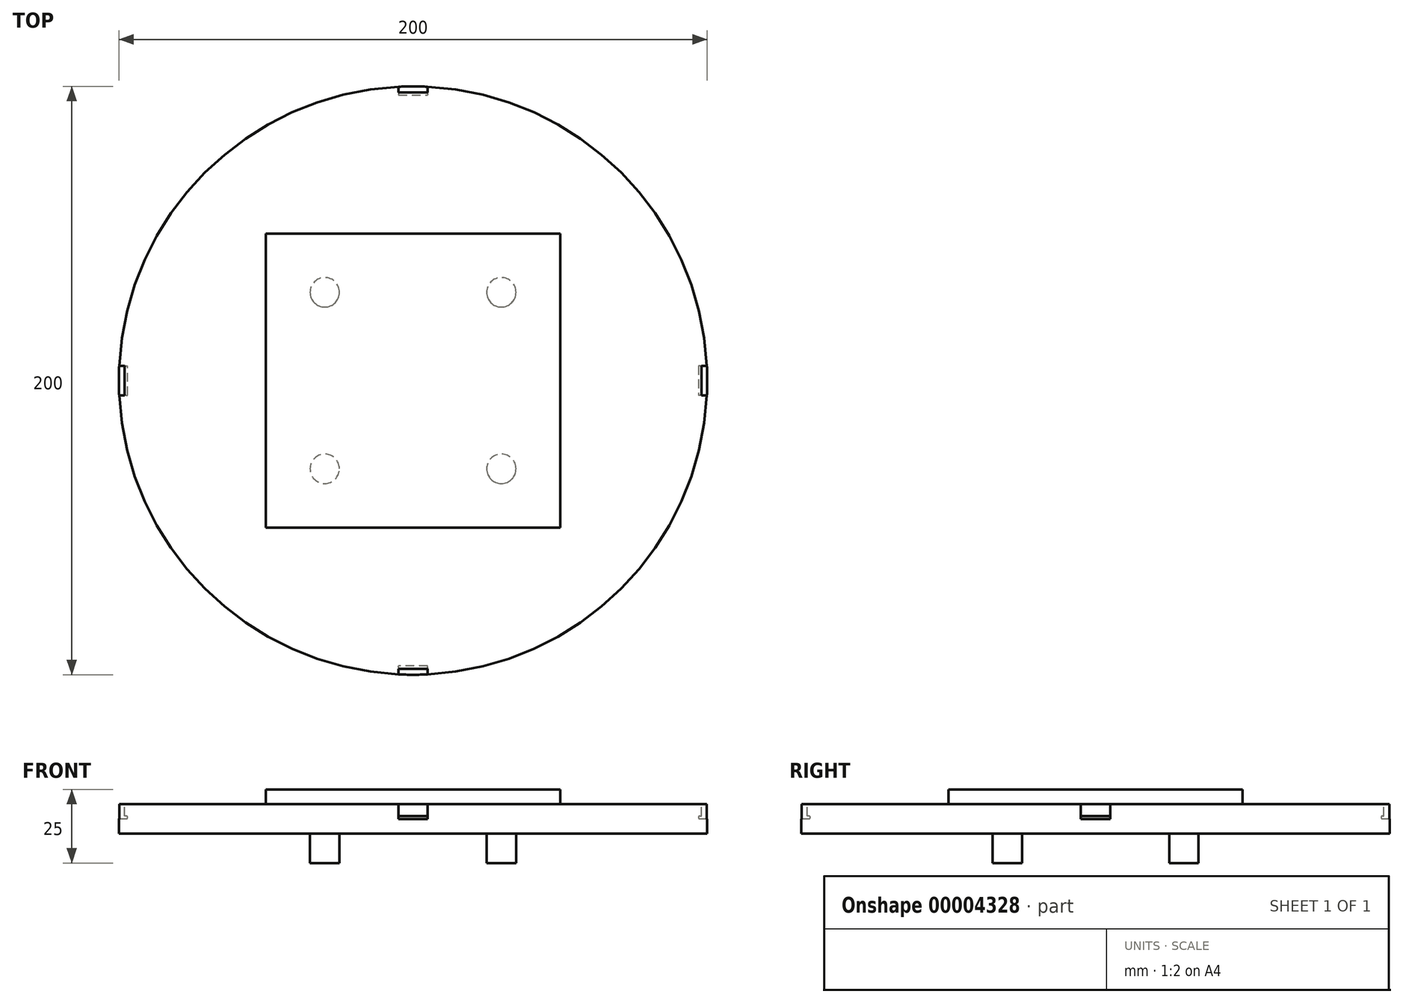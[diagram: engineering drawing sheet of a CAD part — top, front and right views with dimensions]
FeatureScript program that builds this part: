
annotation { "Feature Type Name" : "Feature", "Feature Type Description" : "" }
export const myFeature = defineFeature(function(context is Context, id is Id, definition is map)
    precondition{}
    {
        {
            var Q0;
            Q0=qCreatedBy(makeId("Top.planeOp"),FACE);
            var sketch = newSketch(context, id + "F0", { "sketchPlane" : qUnion([Q0])});
            skCircle(sketch, "E0", {"center": v(0, 0) * mm, "radius": 100 * mm});
            skSolve(sketch);
        }
        {
            var Q0;
            Q0=makeQuery(id+"F0.imprint","IMPRINT",FACE,{"disambiguationData":[TD([[makeQuery(id+"F0.imprint","IMPRINT",EDGE,{"derivedFrom":sQuery(id+"F0.wireOp",EDGE,"E0")}),1.0]])]});
            extrude(context, id + "F1", {"entities" : qUnion([Q0]), "depth" : 10 * mm});
        }
        {
            var Q0;
            Q0=makeQuery(id+"F1.opExtrude","CAP_FACE",FACE,{"disambiguationData":[OSD([sQuery(id+"F0.wireOp",EDGE,"E0")])],"isStart":false});
            var sketch = newSketch(context, id + "F2", { "sketchPlane" : qUnion([Q0])});
            skCircle(sketch, "E1.0", {"center": v(0, 0) * mm, "radius": 90 * mm});
            skLineSegment(sketch, "E2.0", {"start": v(50, 50) * mm, "end": v(-50, 50) * mm});
            skLineSegment(sketch, "E3.0", {"start": v(50, -50) * mm, "end": v(-50, -50) * mm});
            skLineSegment(sketch, "E4.trimOffspring", {"start": v(-50, -50) * mm, "end": v(-50, 50) * mm});
            skLineSegment(sketch, "E5.trimOffspring", {"start": v(50, -50) * mm, "end": v(50, 50) * mm});
            skSolve(sketch);
        }
        {
            var Q0;
            Q0=makeQuery(id+"F1.opExtrude","CAP_FACE",FACE,{"disambiguationData":[OSD([sQuery(id+"F0.wireOp",EDGE,"E0")])],"isStart":false});
            var sketch = newSketch(context, id + "F3", { "sketchPlane" : qUnion([Q0])});
            skLineSegment(sketch, "E6.0", {"start": v(5, -98) * mm, "end": v(-5, -98) * mm});
            skLineSegment(sketch, "E7", {"start": v(-5, -98) * mm, "end": v(-5, -101) * mm});
            skLineSegment(sketch, "E8", {"start": v(5, -98) * mm, "end": v(5, -101) * mm});
            skLineSegment(sketch, "E9.0", {"start": v(-98, 5) * mm, "end": v(-98, -5) * mm});
            skLineSegment(sketch, "E10", {"start": v(-98, 5) * mm, "end": v(-101, 5) * mm});
            skLineSegment(sketch, "E11", {"start": v(-98, -5) * mm, "end": v(-101, -5) * mm});
            skLineSegment(sketch, "E12.0", {"start": v(5, 98) * mm, "end": v(-5, 98) * mm});
            skLineSegment(sketch, "E13", {"start": v(-5, 101) * mm, "end": v(-5, 98) * mm});
            skLineSegment(sketch, "E14", {"start": v(5, 101) * mm, "end": v(5, 98) * mm});
            skLineSegment(sketch, "E15.0", {"start": v(98, 5) * mm, "end": v(98, -5) * mm});
            skLineSegment(sketch, "E16", {"start": v(101, 5) * mm, "end": v(98, 5) * mm});
            skLineSegment(sketch, "E17", {"start": v(101, -5) * mm, "end": v(98, -5) * mm});
            skLineSegment(sketch, "E18.0", {"start": v(-101, 5) * mm, "end": v(-101, -5) * mm});
            skLineSegment(sketch, "E19.0", {"start": v(5, 101) * mm, "end": v(-5, 101) * mm});
            skLineSegment(sketch, "E20.0", {"start": v(101, 5) * mm, "end": v(101, -5) * mm});
            skLineSegment(sketch, "E21.0", {"start": v(5, -101) * mm, "end": v(-5, -101) * mm});
            skSolve(sketch);
        }
        {
            var Q0;
            Q0=makeQuery(id+"F2.imprint","IMPRINT",FACE,{"disambiguationData":[TD([[makeQuery(id+"F2.imprint","IMPRINT",EDGE,{"derivedFrom":sQuery(id+"F2.wireOp",EDGE,"E2.0")}),1.0]])]});
            extrude(context, id + "F4", {"entities" : qUnion([Q0]), "operationType" : NewBodyOperationType.ADD, "depth" : 5 * mm});
        }
        {
            var Q0;
            {var subQ5=sQuery(id+"F3.wireOp",EDGE,"E12.0");Q0=makeQuery(id+"F3.imprint","IMPRINT",FACE,{"disambiguationData":[TD([[makeQuery(id+"F3.imprint","IMPRINT",EDGE,{"derivedFrom":subQ5}),-1.0]])]});}
            var Q1;
            {var subQ5=sQuery(id+"F3.wireOp",EDGE,"E9.0");Q1=makeQuery(id+"F3.imprint","IMPRINT",FACE,{"disambiguationData":[TD([[makeQuery(id+"F3.imprint","IMPRINT",EDGE,{"derivedFrom":subQ5}),-1.0]])]});}
            var Q2;
            {var subQ5=sQuery(id+"F3.wireOp",EDGE,"E6.0");Q2=makeQuery(id+"F3.imprint","IMPRINT",FACE,{"disambiguationData":[TD([[makeQuery(id+"F3.imprint","IMPRINT",EDGE,{"derivedFrom":subQ5}),1.0]])]});}
            var Q3;
            {var subQ5=sQuery(id+"F3.wireOp",EDGE,"E15.0");Q3=makeQuery(id+"F3.imprint","IMPRINT",FACE,{"disambiguationData":[TD([[makeQuery(id+"F3.imprint","IMPRINT",EDGE,{"derivedFrom":subQ5}),1.0]])]});}
            extrude(context, id + "F5", {"entities" : qUnion([Q0, Q1, Q2, Q3]), "operationType" : NewBodyOperationType.REMOVE, "oppositeDirection" : true, "depth" : 5 * mm});
        }
        {
            var Q0;
            Q0=makeQuery(id+"F5.boolean.opBoolean","COPY",FACE,{"derivedFrom":makeQuery(id+"F5.opExtrude","SWEPT_FACE",FACE,{"disambiguationData":[OSD([sQuery(id+"F3.wireOp",EDGE,"E15.0")])]})});
            var sketch = newSketch(context, id + "F6", { "sketchPlane" : qUnion([Q0])});
            skLineSegment(sketch, "E22.0", {"start": v(5, 6) * mm, "end": v(-5, 6) * mm});
            skSolve(sketch);
        }
        {
            var Q0;
            Q0=makeQuery(id+"F5.boolean.opBoolean","COPY",FACE,{"derivedFrom":makeQuery(id+"F5.opExtrude","SWEPT_FACE",FACE,{"disambiguationData":[OSD([sQuery(id+"F3.wireOp",EDGE,"E6.0")])]})});
            var sketch = newSketch(context, id + "F7", { "sketchPlane" : qUnion([Q0])});
            skLineSegment(sketch, "E23.0", {"start": v(5, 6) * mm, "end": v(-5, 6) * mm});
            skSolve(sketch);
        }
        {
            var Q0;
            Q0=makeQuery(id+"F5.boolean.opBoolean","COPY",FACE,{"derivedFrom":makeQuery(id+"F5.opExtrude","SWEPT_FACE",FACE,{"disambiguationData":[OSD([sQuery(id+"F3.wireOp",EDGE,"E9.0")])]})});
            var sketch = newSketch(context, id + "F8", { "sketchPlane" : qUnion([Q0])});
            skLineSegment(sketch, "E24.0", {"start": v(-5, 6) * mm, "end": v(5, 6) * mm});
            skSolve(sketch);
        }
        {
            var Q0;
            Q0=makeQuery(id+"F5.boolean.opBoolean","COPY",FACE,{"derivedFrom":makeQuery(id+"F5.opExtrude","SWEPT_FACE",FACE,{"disambiguationData":[OSD([sQuery(id+"F3.wireOp",EDGE,"E12.0")])]})});
            var sketch = newSketch(context, id + "F9", { "sketchPlane" : qUnion([Q0])});
            skLineSegment(sketch, "E25.0", {"start": v(-5, 6) * mm, "end": v(5, 6) * mm});
            skSolve(sketch);
        }
        {
            var Q0;
            {var subQ2=sQuery(id+"F9.wireOp",EDGE,"E25.0");Q0=makeQuery(id+"F9.imprint","IMPRINT",FACE,{"disambiguationData":[TD([[makeQuery(id+"F9.imprint","IMPRINT",EDGE,{"derivedFrom":subQ2}),-1.0]])]});}
            extrude(context, id + "F10", {"entities" : qUnion([Q0]), "operationType" : NewBodyOperationType.REMOVE, "oppositeDirection" : true, "depth" : 1 * mm});
        }
        {
            var Q0;
            {var subQ2=sQuery(id+"F8.wireOp",EDGE,"E24.0");Q0=makeQuery(id+"F8.imprint","IMPRINT",FACE,{"disambiguationData":[TD([[makeQuery(id+"F8.imprint","IMPRINT",EDGE,{"derivedFrom":subQ2}),-1.0]])]});}
            extrude(context, id + "F11", {"entities" : qUnion([Q0]), "operationType" : NewBodyOperationType.REMOVE, "oppositeDirection" : true, "depth" : 1 * mm});
        }
        {
            var Q0;
            {var subQ2=sQuery(id+"F7.wireOp",EDGE,"E23.0");Q0=makeQuery(id+"F7.imprint","IMPRINT",FACE,{"disambiguationData":[TD([[makeQuery(id+"F7.imprint","IMPRINT",EDGE,{"derivedFrom":subQ2}),1.0]])]});}
            extrude(context, id + "F12", {"entities" : qUnion([Q0]), "operationType" : NewBodyOperationType.REMOVE, "oppositeDirection" : true, "depth" : 1 * mm});
        }
        {
            var Q0;
            {var subQ2=sQuery(id+"F6.wireOp",EDGE,"E22.0");Q0=makeQuery(id+"F6.imprint","IMPRINT",FACE,{"disambiguationData":[TD([[makeQuery(id+"F6.imprint","IMPRINT",EDGE,{"derivedFrom":subQ2}),1.0]])]});}
            extrude(context, id + "F13", {"entities" : qUnion([Q0]), "operationType" : NewBodyOperationType.REMOVE, "oppositeDirection" : true, "depth" : 1 * mm});
        }
        {
            var Q0;
            Q0=makeQuery(id+"F10.boolean.opBoolean","COPY",EDGE,{"derivedFrom":makeQuery(id+"F10.opExtrude","CAP_EDGE",EDGE,{"disambiguationData":[OSD([sQuery(id+"F9.wireOp",EDGE,"E25.0")])],"isStart":false})});
            var Q1;
            Q1=makeQuery(id+"F10.boolean.opBoolean","COPY",EDGE,{"derivedFrom":makeQuery(id+"F10.opExtrude","CAP_EDGE",EDGE,{"disambiguationData":[OSD([sQuery(id+"F3.wireOp",EDGE,"E12.0")])],"isStart":false})});
            fillet(context, id + "F14", {"entities" : qUnion([Q0, Q1]), "radius" : 0.5 * mm, "tangentPropagation" : true, "allowEdgeOverflow" : false});
        }
        {
            var Q0;
            Q0=makeQuery(id+"F13.boolean.opBoolean","COPY",EDGE,{"derivedFrom":makeQuery(id+"F13.opExtrude","CAP_EDGE",EDGE,{"disambiguationData":[OSD([sQuery(id+"F6.wireOp",EDGE,"E22.0")])],"isStart":false})});
            var Q1;
            Q1=makeQuery(id+"F13.boolean.opBoolean","COPY",EDGE,{"derivedFrom":makeQuery(id+"F13.opExtrude","CAP_EDGE",EDGE,{"disambiguationData":[OSD([sQuery(id+"F3.wireOp",EDGE,"E15.0")])],"isStart":false})});
            fillet(context, id + "F15", {"entities" : qUnion([Q0, Q1]), "radius" : 0.5 * mm, "tangentPropagation" : true, "allowEdgeOverflow" : false});
        }
        {
            var Q0;
            Q0=makeQuery(id+"F12.boolean.opBoolean","COPY",EDGE,{"derivedFrom":makeQuery(id+"F12.opExtrude","CAP_EDGE",EDGE,{"disambiguationData":[OSD([sQuery(id+"F7.wireOp",EDGE,"E23.0")])],"isStart":false})});
            var Q1;
            Q1=makeQuery(id+"F12.boolean.opBoolean","COPY",EDGE,{"derivedFrom":makeQuery(id+"F12.opExtrude","CAP_EDGE",EDGE,{"disambiguationData":[OSD([sQuery(id+"F3.wireOp",EDGE,"E6.0")])],"isStart":false})});
            fillet(context, id + "F16", {"entities" : qUnion([Q0, Q1]), "radius" : 0.5 * mm, "tangentPropagation" : true, "allowEdgeOverflow" : false});
        }
        {
            var Q0;
            Q0=makeQuery(id+"F11.boolean.opBoolean","COPY",EDGE,{"derivedFrom":makeQuery(id+"F11.opExtrude","CAP_EDGE",EDGE,{"disambiguationData":[OSD([sQuery(id+"F8.wireOp",EDGE,"E24.0")])],"isStart":false})});
            var Q1;
            Q1=makeQuery(id+"F11.boolean.opBoolean","COPY",EDGE,{"derivedFrom":makeQuery(id+"F11.opExtrude","CAP_EDGE",EDGE,{"disambiguationData":[OSD([sQuery(id+"F3.wireOp",EDGE,"E9.0")])],"isStart":false})});
            fillet(context, id + "F17", {"entities" : qUnion([Q0, Q1]), "radius" : 0.5 * mm, "tangentPropagation" : true, "allowEdgeOverflow" : false});
        }
        {
            var Q0;
            Q0=makeQuery(id+"F1.opExtrude","CAP_FACE",FACE,{"disambiguationData":[OSD([sQuery(id+"F0.wireOp",EDGE,"E0")])],"isStart":true});
            var sketch = newSketch(context, id + "F18", { "sketchPlane" : qUnion([Q0])});
            skLineSegment(sketch, "E26", {"start": v(0, 0) * mm, "end": v(0, 30) * mm});
            skLineSegment(sketch, "E27", {"start": v(0, 0) * mm, "end": v(0, -30) * mm});
            skLineSegment(sketch, "E28", {"start": v(0, 0) * mm, "end": v(-30, 0) * mm});
            skLineSegment(sketch, "E29", {"start": v(0, 0) * mm, "end": v(30, 0) * mm});
            skLineSegment(sketch, "E30.0", {"start": v(30, 0) * mm, "end": v(30, 30) * mm});
            skLineSegment(sketch, "E31.0", {"start": v(-30, 0) * mm, "end": v(-30, 30) * mm});
            skLineSegment(sketch, "E32.0", {"start": v(0, 30) * mm, "end": v(-30, 30) * mm});
            skLineSegment(sketch, "E33.0", {"start": v(0, 30) * mm, "end": v(30, 30) * mm});
            skLineSegment(sketch, "E34.0", {"start": v(-30, 0) * mm, "end": v(-30, -30) * mm});
            skLineSegment(sketch, "E35.0", {"start": v(30, 0) * mm, "end": v(30, -30) * mm});
            skLineSegment(sketch, "E36.0", {"start": v(0, -30) * mm, "end": v(-30, -30) * mm});
            skLineSegment(sketch, "E37.0", {"start": v(0, -30) * mm, "end": v(30, -30) * mm});
            skCircle(sketch, "E38", {"center": v(-30, 30) * mm, "radius": 5 * mm});
            skCircle(sketch, "E39", {"center": v(30, 30) * mm, "radius": 5 * mm});
            skCircle(sketch, "E40", {"center": v(-30, -30) * mm, "radius": 5 * mm});
            skCircle(sketch, "E41", {"center": v(30, -30) * mm, "radius": 5 * mm});
            skSolve(sketch);
        }
        {
            var Q0;
            {var subQ1=sQuery(id+"F18.wireOp",EDGE,"E32.0");var subQ3=sQuery(id+"F18.wireOp",EDGE,"E31.0");var subQ5=makeQuery(id+"F18.imprint","INTERSECT",VERTEX,{"derivedFrom":[subQ3,subQ1]});Q0=makeQuery(id+"F18.imprint","IMPRINT",FACE,{"disambiguationData":[TD([[makeQuery(id+"F18.imprint","IMPRINT",EDGE,{"disambiguationData":[TD([[subQ5,1.0]])],"derivedFrom":subQ3}),1.0]])]});}
            var Q1;
            {var subQ1=sQuery(id+"F18.wireOp",EDGE,"E32.0");var subQ3=sQuery(id+"F18.wireOp",EDGE,"E31.0");var subQ5=makeQuery(id+"F18.imprint","INTERSECT",VERTEX,{"derivedFrom":[subQ3,subQ1]});Q1=makeQuery(id+"F18.imprint","IMPRINT",FACE,{"disambiguationData":[TD([[makeQuery(id+"F18.imprint","IMPRINT",EDGE,{"disambiguationData":[TD([[subQ5,1.0]])],"derivedFrom":subQ3}),-1.0]])]});}
            var Q2;
            {var subQ1=sQuery(id+"F18.wireOp",EDGE,"E33.0");var subQ3=sQuery(id+"F18.wireOp",EDGE,"E30.0");var subQ5=makeQuery(id+"F18.imprint","INTERSECT",VERTEX,{"derivedFrom":[subQ3,subQ1]});Q2=makeQuery(id+"F18.imprint","IMPRINT",FACE,{"disambiguationData":[TD([[makeQuery(id+"F18.imprint","IMPRINT",EDGE,{"disambiguationData":[TD([[subQ5,1.0]])],"derivedFrom":subQ3}),-1.0]])]});}
            var Q3;
            {var subQ1=sQuery(id+"F18.wireOp",EDGE,"E33.0");var subQ3=sQuery(id+"F18.wireOp",EDGE,"E30.0");var subQ5=makeQuery(id+"F18.imprint","INTERSECT",VERTEX,{"derivedFrom":[subQ3,subQ1]});Q3=makeQuery(id+"F18.imprint","IMPRINT",FACE,{"disambiguationData":[TD([[makeQuery(id+"F18.imprint","IMPRINT",EDGE,{"disambiguationData":[TD([[subQ5,1.0]])],"derivedFrom":subQ3}),1.0]])]});}
            var Q4;
            {var subQ1=sQuery(id+"F18.wireOp",EDGE,"E36.0");var subQ3=sQuery(id+"F18.wireOp",EDGE,"E34.0");var subQ5=makeQuery(id+"F18.imprint","INTERSECT",VERTEX,{"derivedFrom":[subQ3,subQ1]});Q4=makeQuery(id+"F18.imprint","IMPRINT",FACE,{"disambiguationData":[TD([[makeQuery(id+"F18.imprint","IMPRINT",EDGE,{"disambiguationData":[TD([[subQ5,1.0]])],"derivedFrom":subQ3}),-1.0]])]});}
            var Q5;
            {var subQ1=sQuery(id+"F18.wireOp",EDGE,"E36.0");var subQ3=sQuery(id+"F18.wireOp",EDGE,"E34.0");var subQ5=makeQuery(id+"F18.imprint","INTERSECT",VERTEX,{"derivedFrom":[subQ3,subQ1]});Q5=makeQuery(id+"F18.imprint","IMPRINT",FACE,{"disambiguationData":[TD([[makeQuery(id+"F18.imprint","IMPRINT",EDGE,{"disambiguationData":[TD([[subQ5,1.0]])],"derivedFrom":subQ3}),1.0]])]});}
            var Q6;
            {var subQ1=sQuery(id+"F18.wireOp",EDGE,"E37.0");var subQ3=sQuery(id+"F18.wireOp",EDGE,"E35.0");var subQ5=makeQuery(id+"F18.imprint","INTERSECT",VERTEX,{"derivedFrom":[subQ3,subQ1]});Q6=makeQuery(id+"F18.imprint","IMPRINT",FACE,{"disambiguationData":[TD([[makeQuery(id+"F18.imprint","IMPRINT",EDGE,{"disambiguationData":[TD([[subQ5,1.0]])],"derivedFrom":subQ3}),-1.0]])]});}
            var Q7;
            {var subQ1=sQuery(id+"F18.wireOp",EDGE,"E37.0");var subQ3=sQuery(id+"F18.wireOp",EDGE,"E35.0");var subQ5=makeQuery(id+"F18.imprint","INTERSECT",VERTEX,{"derivedFrom":[subQ3,subQ1]});Q7=makeQuery(id+"F18.imprint","IMPRINT",FACE,{"disambiguationData":[TD([[makeQuery(id+"F18.imprint","IMPRINT",EDGE,{"disambiguationData":[TD([[subQ5,1.0]])],"derivedFrom":subQ3}),1.0]])]});}
            extrude(context, id + "F19", {"entities" : qUnion([Q0, Q1, Q2, Q3, Q4, Q5, Q6, Q7]), "operationType" : NewBodyOperationType.ADD, "depth" : 10 * mm});
        }
    });
